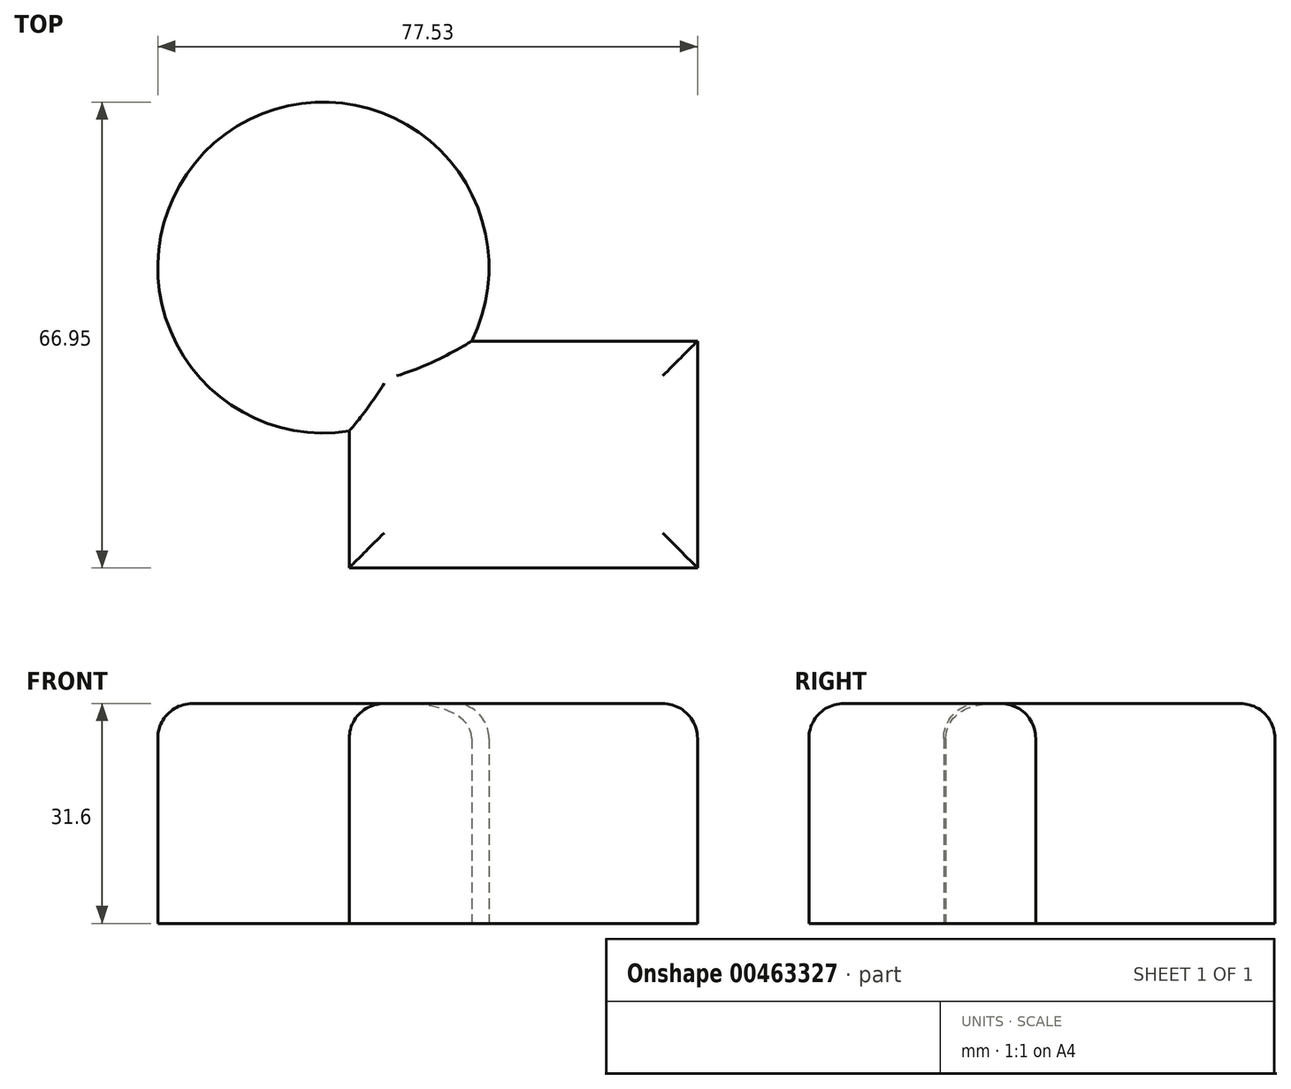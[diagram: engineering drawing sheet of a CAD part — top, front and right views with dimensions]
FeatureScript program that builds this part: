
annotation { "Feature Type Name" : "Feature", "Feature Type Description" : "" }
export const myFeature = defineFeature(function(context is Context, id is Id, definition is map)
    precondition{}
    {
        {
            var Q0;
            Q0=qCreatedBy(makeId("Top.planeOp"),FACE);
            var sketch = newSketch(context, id + "F0", { "sketchPlane" : qUnion([Q0])});
            skArc(sketch, "E0", {"start": v(-15.85, 12.72) * mm, "mid": v(-51.24, 42.47) * mm, "end": v(-33.44, -0.2) * mm});
            skLineSegment(sketch, "E1.bottom", {"start": v(-33.44, -19.87) * mm, "end": v(16.58, -19.87) * mm});
            skLineSegment(sketch, "E1.top", {"start": v(-15.85, 12.72) * mm, "end": v(16.58, 12.72) * mm});
            skLineSegment(sketch, "E1.left", {"start": v(-33.44, -19.87) * mm, "end": v(-33.44, -0.2) * mm});
            skLineSegment(sketch, "E1.right", {"start": v(16.58, -19.87) * mm, "end": v(16.58, 12.72) * mm});
            skSolve(sketch);
        }
        {
            var Q0;
            Q0 = qSketchRegion(id + "F0", true);
            extrude(context, id + "F1", {"entities" : qUnion([Q0]), "depth" : 31.6 * mm});
        }
        {
            var Q0;
            Q0=makeQuery(id+"F1.opExtrude","CAP_FACE",FACE,{"disambiguationData":[OSD([sQuery(id+"F0.wireOp",EDGE,"E0"),sQuery(id+"F0.wireOp",EDGE,"E1.bottom"),sQuery(id+"F0.wireOp",EDGE,"E1.top"),sQuery(id+"F0.wireOp",EDGE,"E1.left"),sQuery(id+"F0.wireOp",EDGE,"E1.right")])],"isStart":false});
            fillet(context, id + "F2", {"entities" : qUnion([Q0]), "radius" : 5 * mm, "tangentPropagation" : true, "allowEdgeOverflow" : false});
        }
    });
